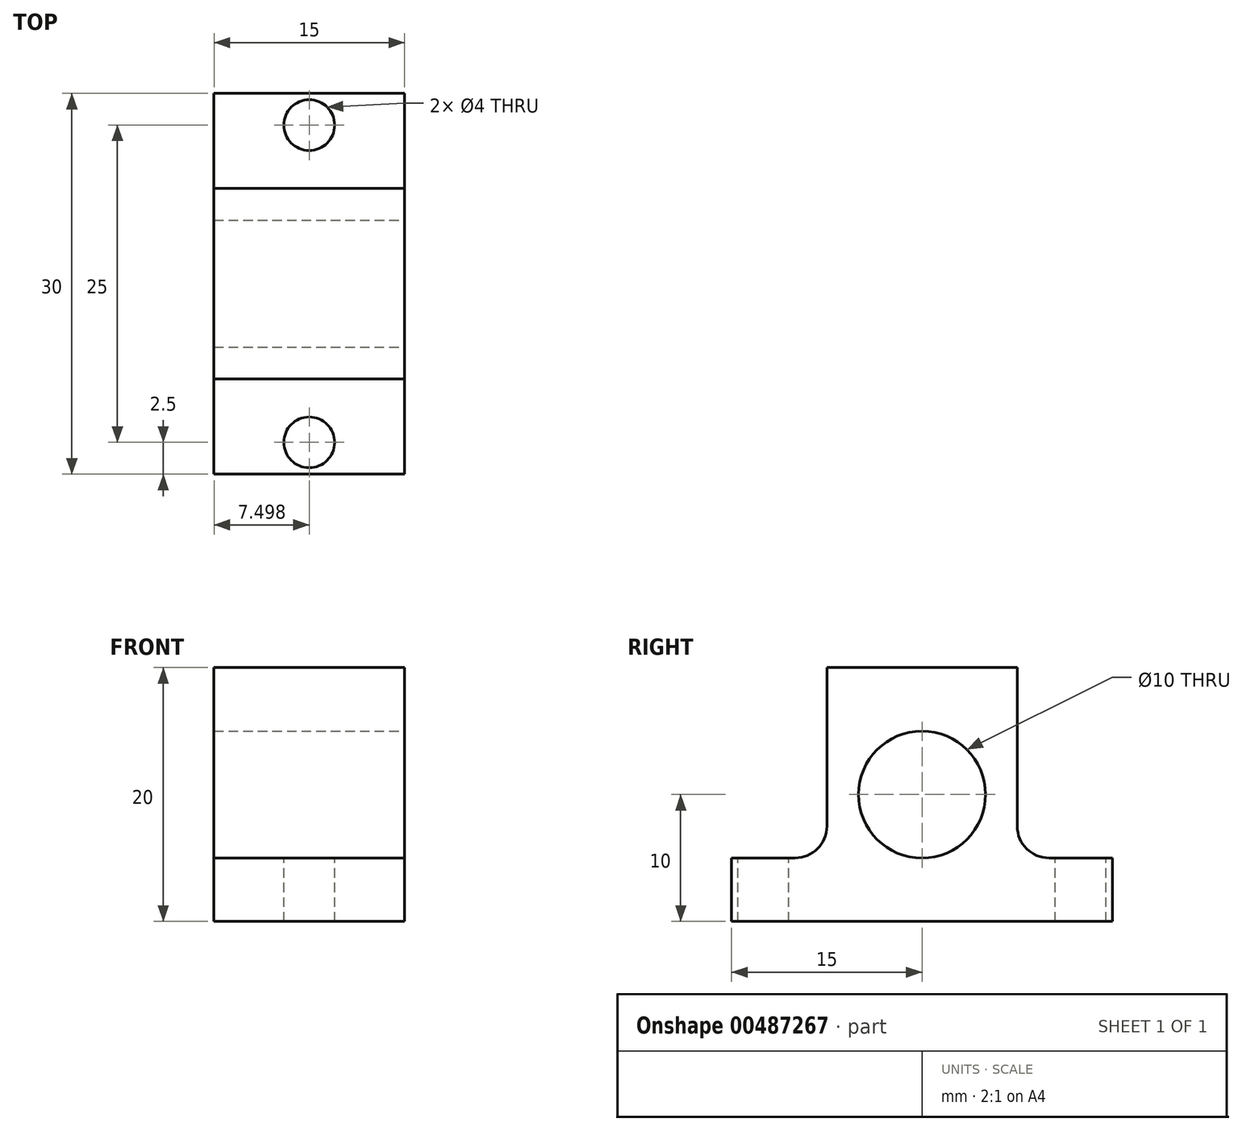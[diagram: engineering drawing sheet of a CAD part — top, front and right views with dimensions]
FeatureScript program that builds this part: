
annotation { "Feature Type Name" : "Feature", "Feature Type Description" : "" }
export const myFeature = defineFeature(function(context is Context, id is Id, definition is map)
    precondition{}
    {
        {
            var Q0;
            Q0=qCreatedBy(makeId("Top.planeOp"),FACE);
            var sketch = newSketch(context, id + "F0", { "sketchPlane" : qUnion([Q0])});
            skLineSegment(sketch, "E0.bottom", {"start": v(-5.2, 4.72) * mm, "end": v(9.8, 4.72) * mm});
            skLineSegment(sketch, "E0.top", {"start": v(-5.2, -25.28) * mm, "end": v(9.8, -25.28) * mm});
            skLineSegment(sketch, "E0.left", {"start": v(-5.2, 4.72) * mm, "end": v(-5.2, -25.28) * mm});
            skLineSegment(sketch, "E0.right", {"start": v(9.8, 4.72) * mm, "end": v(9.8, -25.28) * mm});
            skSolve(sketch);
        }
        {
            var Q0;
            Q0=makeQuery(id+"F0.imprint","IMPRINT",FACE,{"disambiguationData":[TD([[makeQuery(id+"F0.imprint","IMPRINT",EDGE,{"derivedFrom":sQuery(id+"F0.wireOp",EDGE,"E0.bottom")}),-1.0]])]});
            extrude(context, id + "F1", {"entities" : qUnion([Q0]), "depth" : 20 * mm});
        }
        {
            var Q0;
            Q0=makeQuery(id+"F1.opExtrude","SWEPT_FACE",FACE,{"disambiguationData":[OSD([sQuery(id+"F0.wireOp",EDGE,"E0.right")])]});
            var sketch = newSketch(context, id + "F2", { "sketchPlane" : qUnion([Q0])});
            skCircle(sketch, "E1", {"center": v(-10.28, 10) * mm, "radius": 5 * mm});
            skPoint(sketch, "E1.centerSnap0", {"position": v(-10.28, 0) * mm});
            skPoint(sketch, "E1.centerSnap1", {"position": v(4.72, 10) * mm});
            skSolve(sketch);
        }
        {
            var Q0;
            Q0=makeQuery(id+"F2.imprint","IMPRINT",FACE,{"disambiguationData":[TD([[makeQuery(id+"F2.imprint","IMPRINT",EDGE,{"derivedFrom":sQuery(id+"F2.wireOp",EDGE,"E1")}),1.0]])]});
            extrude(context, id + "F3", {"entities" : qUnion([Q0]), "operationType" : NewBodyOperationType.REMOVE, "endBound" : BoundingType.THROUGH_ALL, "oppositeDirection" : true, "depth" : 25 * mm});
        }
        {
            var Q0;
            Q0=makeQuery(id+"F1.opExtrude","SWEPT_FACE",FACE,{"disambiguationData":[OSD([sQuery(id+"F0.wireOp",EDGE,"E0.left")])]});
            var sketch = newSketch(context, id + "F4", { "sketchPlane" : qUnion([Q0])});
            skLineSegment(sketch, "E2", {"start": v(25.28, 0) * mm, "end": v(25.28, 5) * mm});
            skLineSegment(sketch, "E3", {"start": v(25.28, 5) * mm, "end": v(20.28, 5) * mm});
            skLineSegment(sketch, "E4", {"start": v(17.78, 7.5) * mm, "end": v(17.78, 20) * mm});
            skArc(sketch, "E5", {"start": v(17.78, 7.5) * mm, "mid": v(18.51, 5.73) * mm, "end": v(20.28, 5) * mm});
            skSolve(sketch);
        }
        {
            var Q0;
            {var subQ4=sQuery(id+"F4.wireOp",EDGE,"E3");Q0=makeQuery(id+"F4.imprint","IMPRINT",FACE,{"disambiguationData":[TD([[makeQuery(id+"F4.imprint","IMPRINT",EDGE,{"derivedFrom":subQ4}),-1.0]])]});}
            extrude(context, id + "F5", {"entities" : qUnion([Q0]), "operationType" : NewBodyOperationType.REMOVE, "endBound" : BoundingType.THROUGH_ALL, "oppositeDirection" : true, "depth" : 25 * mm});
        }
        {
            var Q0;
            Q0=makeQuery(id+"F1.opExtrude","SWEPT_FACE",FACE,{"disambiguationData":[OSD([sQuery(id+"F0.wireOp",EDGE,"E0.right")])]});
            var sketch = newSketch(context, id + "F6", { "sketchPlane" : qUnion([Q0])});
            skLineSegment(sketch, "E6", {"start": v(4.72, 0) * mm, "end": v(4.72, 5) * mm});
            skLineSegment(sketch, "E7", {"start": v(4.72, 5) * mm, "end": v(-0.28, 5) * mm});
            skLineSegment(sketch, "E8", {"start": v(-2.78, 7.5) * mm, "end": v(-2.78, 20) * mm});
            skArc(sketch, "E9", {"start": v(-2.78, 7.5) * mm, "mid": v(-2.05, 5.73) * mm, "end": v(-0.28, 5) * mm});
            skPoint(sketch, "E10.end.orphan", {"position": v(-2.78, 7.5) * mm});
            skSolve(sketch);
        }
        {
            var Q0;
            {var subQ4=sQuery(id+"F6.wireOp",EDGE,"E7");Q0=makeQuery(id+"F6.imprint","IMPRINT",FACE,{"disambiguationData":[TD([[makeQuery(id+"F6.imprint","IMPRINT",EDGE,{"derivedFrom":subQ4}),-1.0]])]});}
            extrude(context, id + "F7", {"entities" : qUnion([Q0]), "operationType" : NewBodyOperationType.REMOVE, "endBound" : BoundingType.THROUGH_ALL, "oppositeDirection" : true, "depth" : 25 * mm});
        }
        {
            var Q0;
            Q0=makeQuery(id+"F7.boolean.opBoolean","COPY",FACE,{"derivedFrom":makeQuery(id+"F7.opExtrude","SWEPT_FACE",FACE,{"disambiguationData":[OSD([sQuery(id+"F6.wireOp",EDGE,"E7")])]})});
            var sketch = newSketch(context, id + "F8", { "sketchPlane" : qUnion([Q0])});
            skLineSegment(sketch, "E11", {"start": v(9.8, 4.72) * mm, "end": v(2.3, 4.72) * mm});
            skLineSegment(sketch, "E12", {"start": v(9.8, 4.72) * mm, "end": v(9.8, 2.22) * mm});
            skCircle(sketch, "E13", {"center": v(2.3, 2.22) * mm, "radius": 2 * mm});
            skSolve(sketch);
        }
        {
            var Q0;
            Q0=makeQuery(id+"F8.imprint","IMPRINT",FACE,{"disambiguationData":[TD([[makeQuery(id+"F8.imprint","IMPRINT",EDGE,{"derivedFrom":sQuery(id+"F8.wireOp",EDGE,"E13")}),1.0]])]});
            extrude(context, id + "F9", {"entities" : qUnion([Q0]), "operationType" : NewBodyOperationType.REMOVE, "endBound" : BoundingType.THROUGH_ALL, "oppositeDirection" : true, "depth" : 25 * mm});
        }
        {
            var Q0;
            Q0=makeQuery(id+"F5.boolean.opBoolean","COPY",FACE,{"derivedFrom":makeQuery(id+"F5.opExtrude","SWEPT_FACE",FACE,{"disambiguationData":[OSD([sQuery(id+"F4.wireOp",EDGE,"E3")])]})});
            var sketch = newSketch(context, id + "F10", { "sketchPlane" : qUnion([Q0])});
            skLineSegment(sketch, "E14", {"start": v(9.8, -25.28) * mm, "end": v(2.3, -25.28) * mm});
            skLineSegment(sketch, "E15", {"start": v(2.3, -25.28) * mm, "end": v(9.8, -25.28) * mm});
            skLineSegment(sketch, "E16", {"start": v(9.8, -25.28) * mm, "end": v(9.8, -22.78) * mm});
            skCircle(sketch, "E17", {"center": v(2.3, -22.78) * mm, "radius": 2 * mm});
            skSolve(sketch);
        }
        {
            var Q0;
            Q0=makeQuery(id+"F10.imprint","IMPRINT",FACE,{"disambiguationData":[TD([[makeQuery(id+"F10.imprint","IMPRINT",EDGE,{"derivedFrom":sQuery(id+"F10.wireOp",EDGE,"E17")}),1.0]])]});
            extrude(context, id + "F11", {"entities" : qUnion([Q0]), "operationType" : NewBodyOperationType.REMOVE, "endBound" : BoundingType.THROUGH_ALL, "oppositeDirection" : true, "depth" : 25 * mm});
        }
    });
